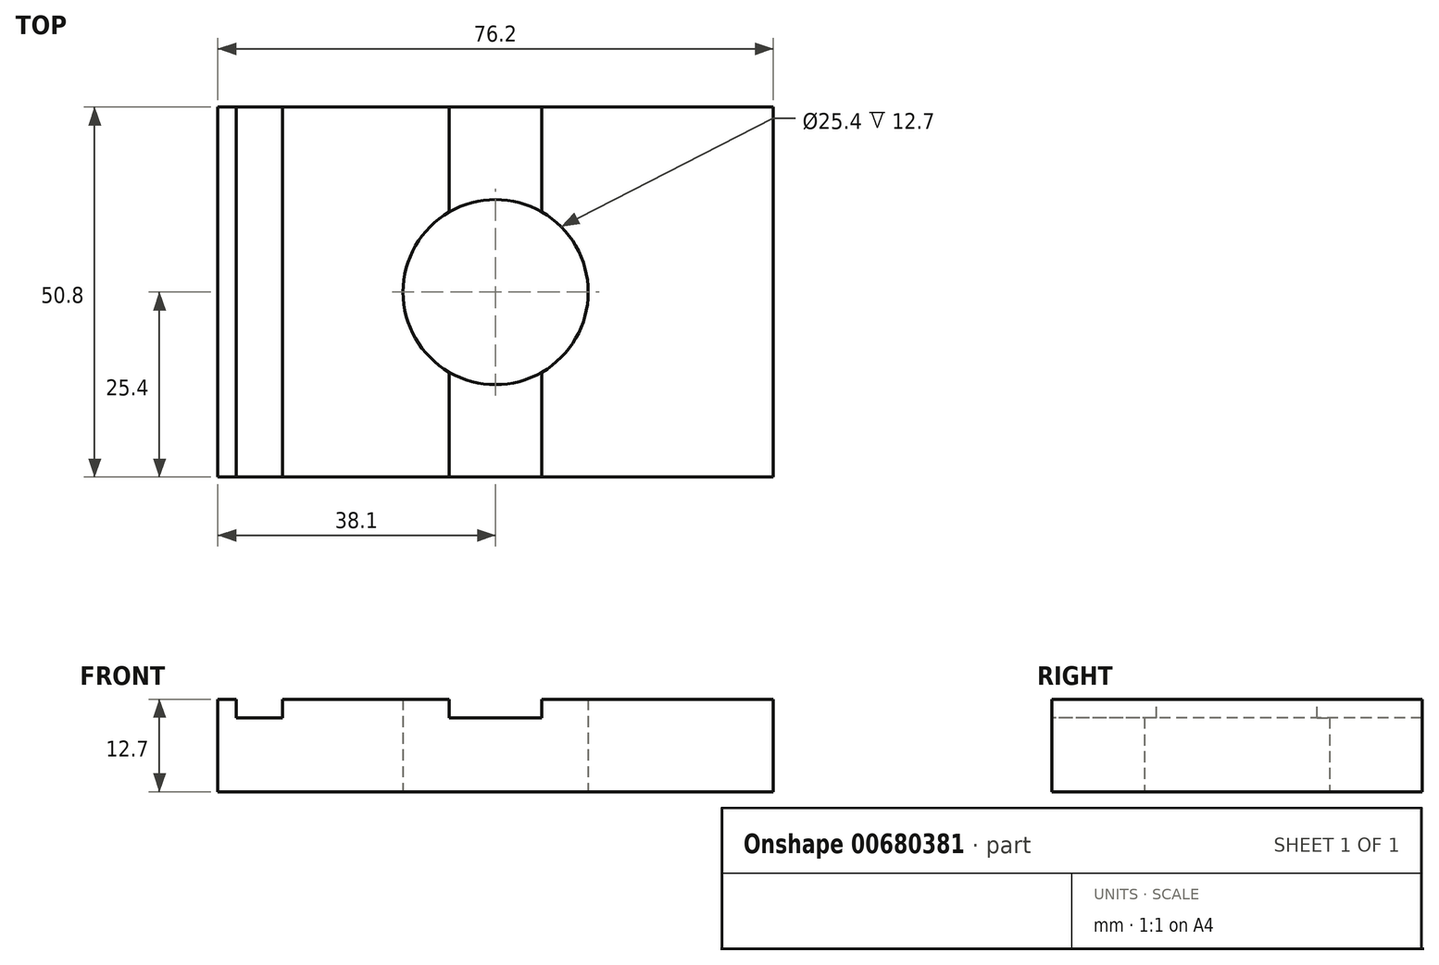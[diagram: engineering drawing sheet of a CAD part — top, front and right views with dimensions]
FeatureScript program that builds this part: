
annotation { "Feature Type Name" : "Feature", "Feature Type Description" : "" }
export const myFeature = defineFeature(function(context is Context, id is Id, definition is map)
    precondition{}
    {
        {
            var Q0;
            Q0=qCreatedBy(makeId("Top.planeOp"),FACE);
            var sketch = newSketch(context, id + "F0", { "sketchPlane" : qUnion([Q0])});
            skLineSegment(sketch, "E0.bottom", {"start": v(38.1, -25.4) * mm, "end": v(-38.1, -25.4) * mm});
            skLineSegment(sketch, "E0.top", {"start": v(38.1, 25.4) * mm, "end": v(-38.1, 25.4) * mm});
            skLineSegment(sketch, "E0.left", {"start": v(38.1, -25.4) * mm, "end": v(38.1, 25.4) * mm});
            skLineSegment(sketch, "E0.right", {"start": v(-38.1, -25.4) * mm, "end": v(-38.1, 25.4) * mm});
            skPoint(sketch, "E0.middle", {"position": v(0, 0) * mm});
            skCircle(sketch, "E1", {"center": v(0, 0) * mm, "radius": 12.7 * mm});
            skSolve(sketch);
        }
        {
            var Q0;
            Q0=makeQuery(id+"F0.imprint","IMPRINT",FACE,{"disambiguationData":[TD([[makeQuery(id+"F0.imprint","IMPRINT",EDGE,{"derivedFrom":sQuery(id+"F0.wireOp",EDGE,"E0.bottom")}),-1.0]])]});
            extrude(context, id + "F1", {"entities" : qUnion([Q0]), "depth" : 12.7 * mm, "offsetDistance" : 25 * mm});
        }
        {
            var Q0;
            Q0=makeQuery(id+"F1.opExtrude","CAP_FACE",FACE,{"disambiguationData":[OSD([sQuery(id+"F0.wireOp",EDGE,"E0.bottom"),sQuery(id+"F0.wireOp",EDGE,"E0.top"),sQuery(id+"F0.wireOp",EDGE,"E0.left"),sQuery(id+"F0.wireOp",EDGE,"E0.right"),sQuery(id+"F0.wireOp",EDGE,"E1")])],"isStart":false});
            var sketch = newSketch(context, id + "F2", { "sketchPlane" : qUnion([Q0])});
            skLineSegment(sketch, "E2.bottom", {"start": v(-35.56, 25.4) * mm, "end": v(-29.2, 25.4) * mm});
            skLineSegment(sketch, "E2.top", {"start": v(-35.56, -25.4) * mm, "end": v(-29.2, -25.4) * mm});
            skLineSegment(sketch, "E2.left", {"start": v(-35.56, 25.4) * mm, "end": v(-35.56, -25.4) * mm});
            skLineSegment(sketch, "E2.right", {"start": v(-29.2, 25.4) * mm, "end": v(-29.2, -25.4) * mm});
            skLineSegment(sketch, "E3", {"start": v(-6.35, 25.4) * mm, "end": v(-6.35, -25.4) * mm});
            skLineSegment(sketch, "E4", {"start": v(6.35, -25.4) * mm, "end": v(6.35, 25.4) * mm});
            skLineSegment(sketch, "E5", {"start": v(6.35, 25.4) * mm, "end": v(-6.35, 25.4) * mm});
            skPoint(sketch, "E6", {"position": v(0, 0) * mm});
            skLineSegment(sketch, "E7", {"start": v(0, 25.4) * mm, "end": v(0, -25.4) * mm, "construction": true});
            skSolve(sketch);
        }
        {
            var Q0;
            Q0=makeQuery(id+"F2.imprint","IMPRINT",FACE,{"disambiguationData":[TD([[makeQuery(id+"F2.imprint","IMPRINT",EDGE,{"derivedFrom":sQuery(id+"F2.wireOp",EDGE,"E2.bottom")}),1.0]])]});
            var Q1;
            {var subQ0=sQuery(id+"F2.wireOp",EDGE,"E5");Q1=makeQuery(id+"F2.imprint","IMPRINT",FACE,{"disambiguationData":[TD([[makeQuery(id+"F2.imprint","IMPRINT",EDGE,{"derivedFrom":subQ0}),1.0]])]});}
            var Q2;
            {var subQ0=sQuery(id+"F2.wireOp",EDGE,"E3");var subQ1=makeQuery(id+"F1.opExtrude","CAP_EDGE",EDGE,{"disambiguationData":[OSD([sQuery(id+"F0.wireOp",EDGE,"E0.bottom")])],"isStart":false});var subQ2=makeQuery(id+"F2.imprint","INTERSECT",VERTEX,{"derivedFrom":[subQ1,subQ0]});Q2=makeQuery(id+"F2.imprint","IMPRINT",FACE,{"disambiguationData":[TD([[makeQuery(id+"F2.imprint","IMPRINT",EDGE,{"disambiguationData":[TD([[subQ2,1.0]])],"derivedFrom":subQ0}),1.0]])]});}
            extrude(context, id + "F3", {"entities" : qUnion([Q0, Q1, Q2]), "operationType" : NewBodyOperationType.REMOVE, "oppositeDirection" : true, "depth" : 2.54 * mm, "offsetDistance" : 25.4 * mm});
        }
    });
